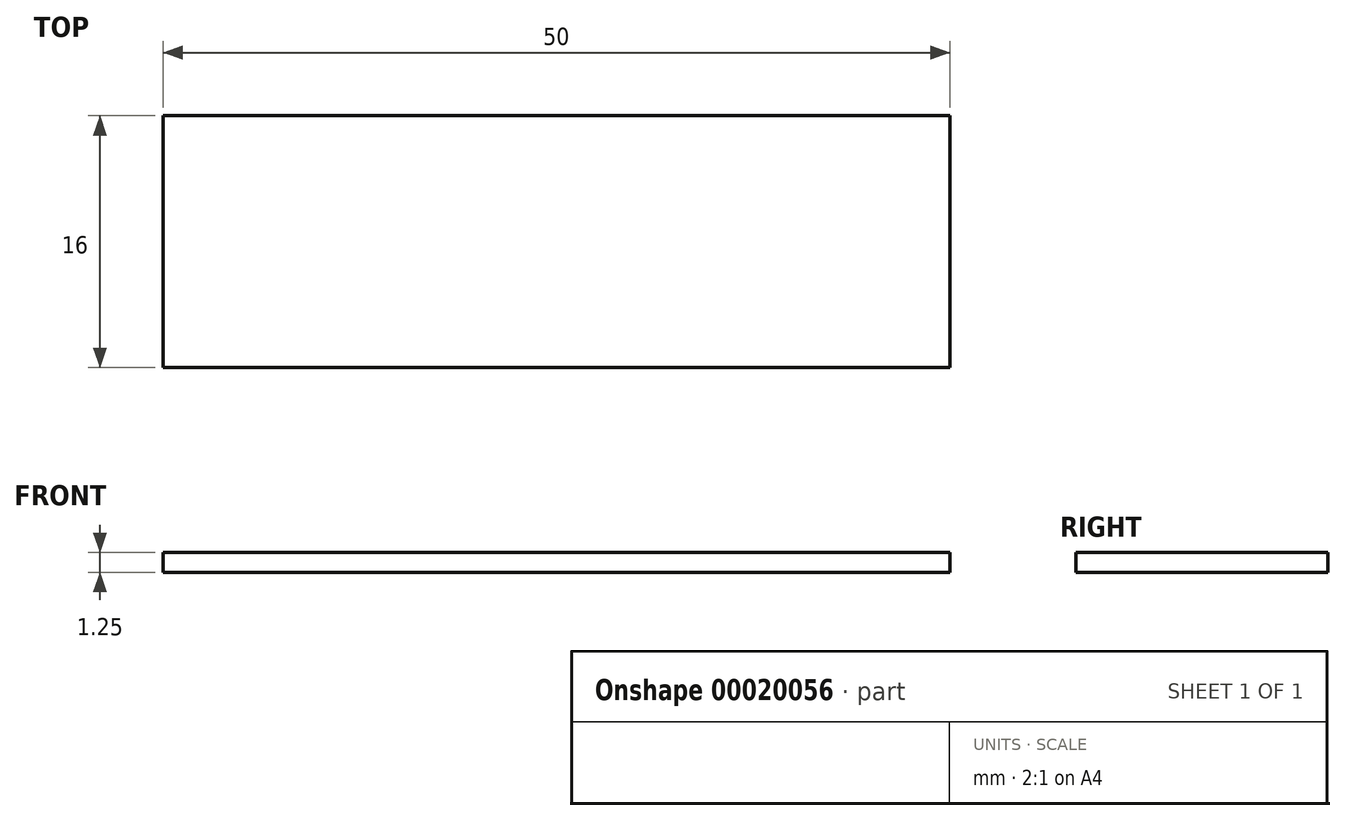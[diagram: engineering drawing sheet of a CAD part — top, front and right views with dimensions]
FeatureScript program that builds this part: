
annotation { "Feature Type Name" : "Feature", "Feature Type Description" : "" }
export const myFeature = defineFeature(function(context is Context, id is Id, definition is map)
    precondition{}
    {
        {
            var Q0;
            Q0=qCreatedBy(makeId("Top.planeOp"),FACE);
            var sketch = newSketch(context, id + "F0", { "sketchPlane" : qUnion([Q0])});
            skLineSegment(sketch, "E0.bottom", {"start": v(-11.84, 7.46) * mm, "end": v(38.16, 7.46) * mm});
            skLineSegment(sketch, "E0.top", {"start": v(-11.84, -8.54) * mm, "end": v(38.16, -8.54) * mm});
            skLineSegment(sketch, "E0.left", {"start": v(-11.84, 7.46) * mm, "end": v(-11.84, -8.54) * mm});
            skLineSegment(sketch, "E0.right", {"start": v(38.16, 7.46) * mm, "end": v(38.16, -8.54) * mm});
            skSolve(sketch);
        }
        {
            var Q0;
            Q0 = qSketchRegion(id + "F0", true);
            extrude(context, id + "F1", {"entities" : qUnion([Q0]), "depth" : 1.25 * mm});
        }
    });
